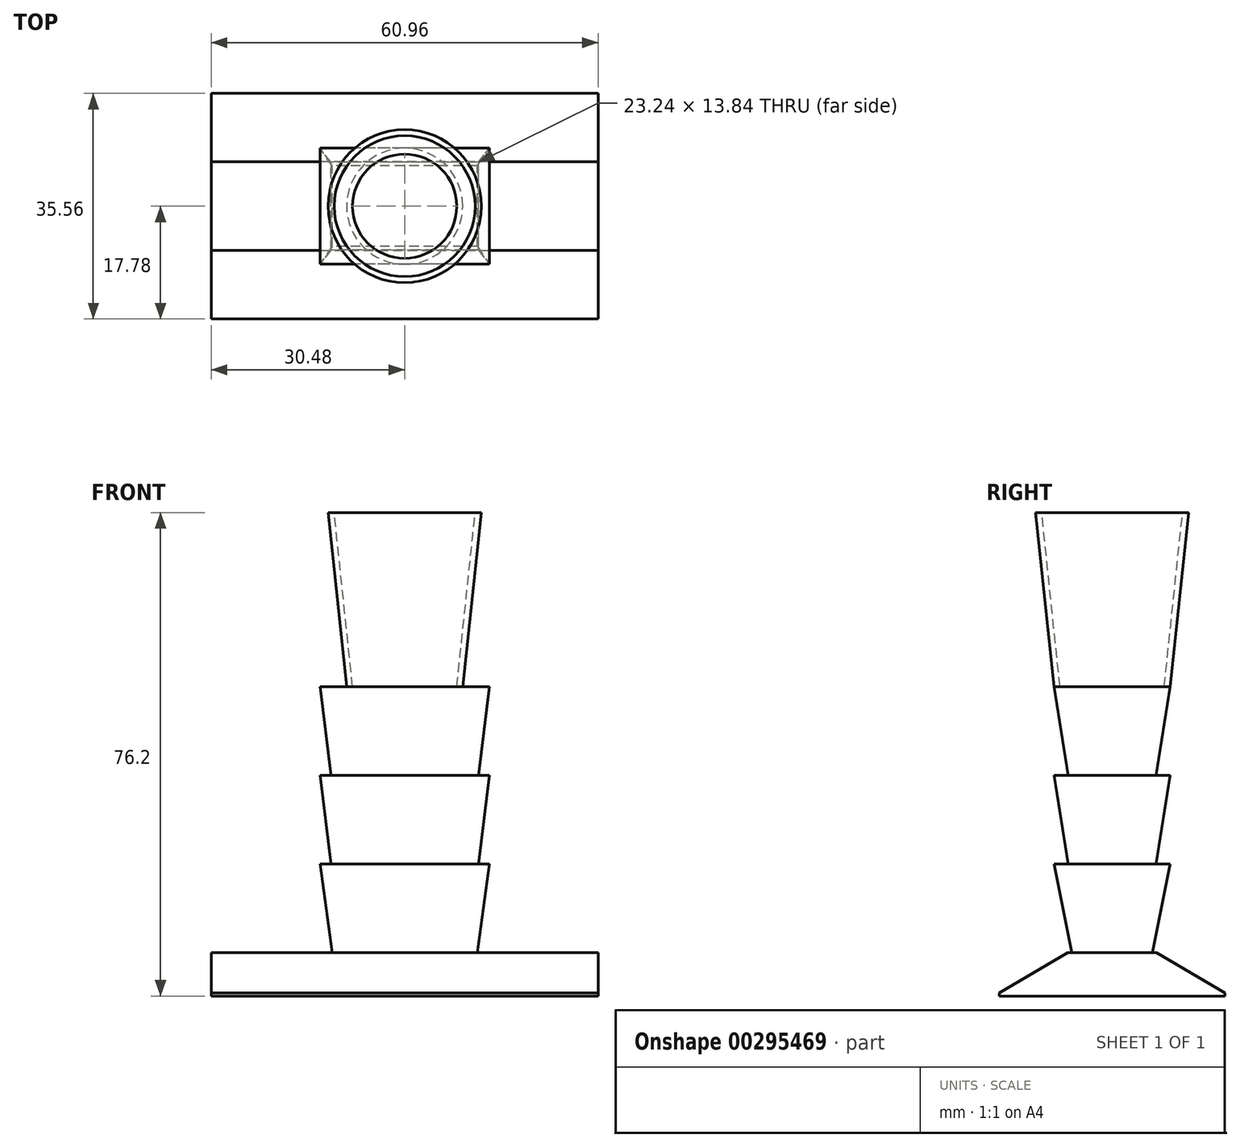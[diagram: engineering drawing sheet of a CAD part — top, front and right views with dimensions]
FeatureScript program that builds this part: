
annotation { "Feature Type Name" : "Feature", "Feature Type Description" : "" }
export const myFeature = defineFeature(function(context is Context, id is Id, definition is map)
    precondition{}
    {
        {
            var Q0;
            Q0=qCreatedBy(makeId("Top.planeOp"),FACE);
            var sketch = newSketch(context, id + "F0", { "sketchPlane" : qUnion([Q0])});
            skLineSegment(sketch, "E0.bottom", {"start": v(30.48, -17.78) * mm, "end": v(-30.48, -17.78) * mm});
            skLineSegment(sketch, "E0.top", {"start": v(30.48, 17.78) * mm, "end": v(-30.48, 17.78) * mm});
            skLineSegment(sketch, "E0.left", {"start": v(30.48, -17.78) * mm, "end": v(30.48, 17.78) * mm});
            skLineSegment(sketch, "E0.right", {"start": v(-30.48, -17.78) * mm, "end": v(-30.48, 17.78) * mm});
            skPoint(sketch, "E0.middle", {"position": v(0, 0) * mm});
            skSolve(sketch);
        }
        {
            var Q0;
            Q0=makeQuery(id+"F0.imprint","IMPRINT",FACE,{"disambiguationData":[TD([[makeQuery(id+"F0.imprint","IMPRINT",EDGE,{"derivedFrom":sQuery(id+"F0.wireOp",EDGE,"E0.bottom")}),-1.0]])]});
            extrude(context, id + "F1", {"entities" : qUnion([Q0]), "depth" : 6.86 * mm});
        }
        {
            var Q0;
            Q0=makeQuery(id+"F1.opExtrude","CAP_EDGE",EDGE,{"disambiguationData":[OSD([sQuery(id+"F0.wireOp",EDGE,"E0.top")])],"isStart":false});
            var Q1;
            Q1=makeQuery(id+"F1.opExtrude","CAP_EDGE",EDGE,{"disambiguationData":[OSD([sQuery(id+"F0.wireOp",EDGE,"E0.bottom")])],"isStart":false});
            chamfer(context, id + "F2", {"entities" : qUnion([Q0, Q1]), "chamferType" : ChamferType.TWO_OFFSETS, "width1" : 10.8 * mm, "oppositeDirection" : false, "width2" : 6.38 * mm, "tangentPropagation" : true});
        }
        {
            var Q0;
            Q0=makeQuery(id+"F1.opExtrude","CAP_FACE",FACE,{"disambiguationData":[OSD([sQuery(id+"F0.wireOp",EDGE,"E0.bottom"),sQuery(id+"F0.wireOp",EDGE,"E0.top"),sQuery(id+"F0.wireOp",EDGE,"E0.left"),sQuery(id+"F0.wireOp",EDGE,"E0.right")])],"isStart":false});
            var sketch = newSketch(context, id + "F3", { "sketchPlane" : qUnion([Q0])});
            skLineSegment(sketch, "E1.bottom", {"start": v(11.43, -6.35) * mm, "end": v(-11.43, -6.35) * mm});
            skLineSegment(sketch, "E1.top", {"start": v(11.43, 6.35) * mm, "end": v(-11.43, 6.35) * mm});
            skLineSegment(sketch, "E1.left", {"start": v(11.43, -6.35) * mm, "end": v(11.43, 6.35) * mm});
            skLineSegment(sketch, "E1.right", {"start": v(-11.43, -6.35) * mm, "end": v(-11.43, 6.35) * mm});
            skPoint(sketch, "E1.middle", {"position": v(0, 0) * mm});
            skSolve(sketch);
        }
        {
            var Q0;
            Q0=makeQuery(id+"F3.imprint","IMPRINT",FACE,{"disambiguationData":[TD([[makeQuery(id+"F3.imprint","IMPRINT",EDGE,{"derivedFrom":sQuery(id+"F3.wireOp",EDGE,"E1.bottom")}),-1.0]])]});
            cPlane(context, id + "F4", {"entities" : qUnion([Q0]), "cplaneType" : CPlaneType.OFFSET, "offset" : 13.97 * mm, "width" : 152.4 * mm, "height" : 152.4 * mm});
        }
        {
            var Q0;
            Q0=qCreatedBy(id+"F4.planeOp",FACE);
            var sketch = newSketch(context, id + "F5", { "sketchPlane" : qUnion([Q0])});
            skLineSegment(sketch, "E2.bottom", {"start": v(13.34, -9.14) * mm, "end": v(-13.34, -9.14) * mm});
            skLineSegment(sketch, "E2.top", {"start": v(13.33, 9.14) * mm, "end": v(-13.34, 9.14) * mm});
            skLineSegment(sketch, "E2.left", {"start": v(13.34, -9.14) * mm, "end": v(13.33, 9.14) * mm});
            skLineSegment(sketch, "E2.right", {"start": v(-13.33, -9.14) * mm, "end": v(-13.34, 9.14) * mm});
            skPoint(sketch, "E2.middle", {"position": v(0, 0) * mm});
            skSolve(sketch);
        }
        {
            var Q1;
            Q1=makeQuery(id+"F3.imprint","IMPRINT",FACE,{"disambiguationData":[TD([[makeQuery(id+"F3.imprint","IMPRINT",EDGE,{"derivedFrom":sQuery(id+"F3.wireOp",EDGE,"E1.bottom")}),-1.0]])]});
            var Q2;
            Q2=makeQuery(id+"F5.imprint","IMPRINT",FACE,{"disambiguationData":[TD([[makeQuery(id+"F5.imprint","IMPRINT",EDGE,{"derivedFrom":sQuery(id+"F5.wireOp",EDGE,"E2.bottom")}),-1.0]])]});
            loft(context, id + "F6", {"operationType" : NewBodyOperationType.ADD, "sheetProfilesArray" : [{ "sheetProfileEntities" : qUnion([Q1]) }, { "sheetProfileEntities" : qUnion([Q2]) }]});
        }
        {
            var Q0;
            Q0=makeQuery(id+"F6.opLoft","CAP_FACE",FACE,{"disambiguationData":[OSD([makeQuery(id+"F5.imprint","IMPRINT",FACE,{"disambiguationData":[TD([[makeQuery(id+"F5.imprint","IMPRINT",EDGE,{"derivedFrom":sQuery(id+"F5.wireOp",EDGE,"E2.bottom")}),-1.0]])]})])],"isStart":true});
            cPlane(context, id + "F7", {"entities" : qUnion([Q0]), "cplaneType" : CPlaneType.OFFSET, "offset" : 13.97 * mm, "width" : 152.4 * mm, "height" : 152.4 * mm});
        }
        {
            var Q0;
            Q0=makeQuery(id+"F6.opLoft","CAP_FACE",FACE,{"disambiguationData":[OSD([makeQuery(id+"F5.imprint","IMPRINT",FACE,{"disambiguationData":[TD([[makeQuery(id+"F5.imprint","IMPRINT",EDGE,{"derivedFrom":sQuery(id+"F5.wireOp",EDGE,"E2.bottom")}),-1.0]])]})])],"isStart":true});
            var sketch = newSketch(context, id + "F8", { "sketchPlane" : qUnion([Q0])});
            skLineSegment(sketch, "E3.bottom", {"start": v(11.62, -6.92) * mm, "end": v(-11.62, -6.92) * mm});
            skLineSegment(sketch, "E3.top", {"start": v(11.62, 6.92) * mm, "end": v(-11.62, 6.92) * mm});
            skLineSegment(sketch, "E3.left", {"start": v(11.62, -6.92) * mm, "end": v(11.62, 6.92) * mm});
            skLineSegment(sketch, "E3.right", {"start": v(-11.62, -6.92) * mm, "end": v(-11.62, 6.92) * mm});
            skPoint(sketch, "E3.middle", {"position": v(0, 0) * mm});
            skSolve(sketch);
        }
        {
            var Q0;
            Q0=qCreatedBy(id+"F7.planeOp",FACE);
            var sketch = newSketch(context, id + "F9", { "sketchPlane" : qUnion([Q0])});
            skLineSegment(sketch, "E4.bottom", {"start": v(13.33, -9.14) * mm, "end": v(-13.34, -9.14) * mm});
            skLineSegment(sketch, "E4.top", {"start": v(13.34, 9.14) * mm, "end": v(-13.34, 9.14) * mm});
            skLineSegment(sketch, "E4.left", {"start": v(13.33, -9.14) * mm, "end": v(13.33, 9.14) * mm});
            skLineSegment(sketch, "E4.right", {"start": v(-13.34, -9.14) * mm, "end": v(-13.34, 9.14) * mm});
            skPoint(sketch, "E4.middle", {"position": v(0, 0) * mm});
            skSolve(sketch);
        }
        {
            var Q1;
            Q1=makeQuery(id+"F8.imprint","IMPRINT",FACE,{"disambiguationData":[TD([[makeQuery(id+"F8.imprint","IMPRINT",EDGE,{"derivedFrom":sQuery(id+"F8.wireOp",EDGE,"E3.bottom")}),-1.0]])]});
            var Q2;
            Q2=makeQuery(id+"F9.imprint","IMPRINT",FACE,{"disambiguationData":[TD([[makeQuery(id+"F9.imprint","IMPRINT",EDGE,{"derivedFrom":sQuery(id+"F9.wireOp",EDGE,"E4.bottom")}),-1.0]])]});
            loft(context, id + "F10", {"operationType" : NewBodyOperationType.ADD, "sheetProfilesArray" : [{ "sheetProfileEntities" : qUnion([Q1]) }, { "sheetProfileEntities" : qUnion([Q2]) }]});
        }
        {
            var Q0;
            Q0=makeQuery(id+"F10.opLoft","CAP_FACE",FACE,{"disambiguationData":[OSD([makeQuery(id+"F9.imprint","IMPRINT",FACE,{"disambiguationData":[TD([[makeQuery(id+"F9.imprint","IMPRINT",EDGE,{"derivedFrom":sQuery(id+"F9.wireOp",EDGE,"E4.bottom")}),-1.0]])]})])],"isStart":true});
            cPlane(context, id + "F11", {"entities" : qUnion([Q0]), "cplaneType" : CPlaneType.OFFSET, "offset" : 13.97 * mm, "width" : 152.4 * mm, "height" : 152.4 * mm});
        }
        {
            var Q0;
            Q0=makeQuery(id+"F10.opLoft","CAP_FACE",FACE,{"disambiguationData":[OSD([makeQuery(id+"F9.imprint","IMPRINT",FACE,{"disambiguationData":[TD([[makeQuery(id+"F9.imprint","IMPRINT",EDGE,{"derivedFrom":sQuery(id+"F9.wireOp",EDGE,"E4.bottom")}),-1.0]])]})])],"isStart":true});
            var sketch = newSketch(context, id + "F12", { "sketchPlane" : qUnion([Q0])});
            skLineSegment(sketch, "E5.bottom", {"start": v(11.62, -6.92) * mm, "end": v(-11.62, -6.92) * mm});
            skLineSegment(sketch, "E5.top", {"start": v(11.62, 6.92) * mm, "end": v(-11.62, 6.92) * mm});
            skLineSegment(sketch, "E5.left", {"start": v(11.62, -6.92) * mm, "end": v(11.62, 6.92) * mm});
            skLineSegment(sketch, "E5.right", {"start": v(-11.62, -6.92) * mm, "end": v(-11.62, 6.92) * mm});
            skPoint(sketch, "E5.middle", {"position": v(0, 0) * mm});
            skSolve(sketch);
        }
        {
            var Q0;
            Q0=qCreatedBy(id+"F11.planeOp",FACE);
            var sketch = newSketch(context, id + "F13", { "sketchPlane" : qUnion([Q0])});
            skLineSegment(sketch, "E6.bottom", {"start": v(13.33, -9.14) * mm, "end": v(-13.34, -9.14) * mm});
            skLineSegment(sketch, "E6.top", {"start": v(13.33, 9.14) * mm, "end": v(-13.34, 9.14) * mm});
            skLineSegment(sketch, "E6.left", {"start": v(13.33, -9.14) * mm, "end": v(13.33, 9.14) * mm});
            skLineSegment(sketch, "E6.right", {"start": v(-13.34, -9.14) * mm, "end": v(-13.34, 9.14) * mm});
            skPoint(sketch, "E6.middle", {"position": v(0, 0) * mm});
            skSolve(sketch);
        }
        {
            var Q1;
            Q1=makeQuery(id+"F12.imprint","IMPRINT",FACE,{"disambiguationData":[TD([[makeQuery(id+"F12.imprint","IMPRINT",EDGE,{"derivedFrom":sQuery(id+"F12.wireOp",EDGE,"E5.bottom")}),-1.0]])]});
            var Q2;
            Q2=makeQuery(id+"F13.imprint","IMPRINT",FACE,{"disambiguationData":[TD([[makeQuery(id+"F13.imprint","IMPRINT",EDGE,{"derivedFrom":sQuery(id+"F13.wireOp",EDGE,"E6.bottom")}),-1.0]])]});
            loft(context, id + "F14", {"operationType" : NewBodyOperationType.ADD, "sheetProfilesArray" : [{ "sheetProfileEntities" : qUnion([Q1]) }, { "sheetProfileEntities" : qUnion([Q2]) }]});
        }
        {
            var Q0;
            Q0=makeQuery(id+"F14.opLoft","CAP_FACE",FACE,{"disambiguationData":[OSD([makeQuery(id+"F13.imprint","IMPRINT",FACE,{"disambiguationData":[TD([[makeQuery(id+"F13.imprint","IMPRINT",EDGE,{"derivedFrom":sQuery(id+"F13.wireOp",EDGE,"E6.bottom")}),-1.0]])]})])],"isStart":true});
            var sketch = newSketch(context, id + "F15", { "sketchPlane" : qUnion([Q0])});
            skLineSegment(sketch, "E7.0.0", {"start": v(13.33, -9.14) * mm, "end": v(13.33, 9.14) * mm});
            skLineSegment(sketch, "E7.0.1", {"start": v(13.33, 9.14) * mm, "end": v(-13.34, 9.14) * mm});
            skLineSegment(sketch, "E7.0.2", {"start": v(-13.34, 9.14) * mm, "end": v(-13.34, -9.14) * mm});
            skLineSegment(sketch, "E7.0.3", {"start": v(-13.34, -9.14) * mm, "end": v(13.33, -9.14) * mm});
            skCircle(sketch, "E8", {"center": v(0, 0) * mm, "radius": 9.14 * mm});
            skSolve(sketch);
        }
        {
            var Q0;
            {var subQ0=sQuery(id+"F15.wireOp",EDGE,"E7.0.2");Q0=makeQuery(id+"F15.imprint","IMPRINT",FACE,{"disambiguationData":[TD([[makeQuery(id+"F15.imprint","IMPRINT",EDGE,{"derivedFrom":subQ0}),1.0]])]});}
            cPlane(context, id + "F16", {"entities" : qUnion([Q0]), "cplaneType" : CPlaneType.OFFSET, "offset" : 27.43 * mm, "width" : 152.4 * mm, "height" : 152.4 * mm});
        }
        {
            var Q0;
            Q0=qCreatedBy(id+"F16.planeOp",FACE);
            var sketch = newSketch(context, id + "F17", { "sketchPlane" : qUnion([Q0])});
            skCircle(sketch, "E9", {"center": v(0, 0) * mm, "radius": 12.07 * mm});
            skSolve(sketch);
        }
        {
            var Q1;
            {var subQ0=sQuery(id+"F15.wireOp",EDGE,"E8");var subQ1=makeQuery(id+"F15.imprint","INTERSECT",VERTEX,{"derivedFrom":[sQuery(id+"F15.wireOp",EDGE,"E7.0.1"),subQ0]});Q1=makeQuery(id+"F15.imprint","IMPRINT",FACE,{"disambiguationData":[TD([[makeQuery(id+"F15.imprint","IMPRINT",EDGE,{"disambiguationData":[TD([[subQ1,-1.0]])],"derivedFrom":subQ0}),1.0]])]});}
            var Q2;
            Q2=makeQuery(id+"F17.imprint","IMPRINT",FACE,{"disambiguationData":[TD([[makeQuery(id+"F17.imprint","IMPRINT",EDGE,{"derivedFrom":sQuery(id+"F17.wireOp",EDGE,"E9")}),1.0]])]});
            loft(context, id + "F18", {"operationType" : NewBodyOperationType.ADD, "sheetProfilesArray" : [{ "sheetProfileEntities" : qUnion([Q1]) }, { "sheetProfileEntities" : qUnion([Q2]) }]});
        }
        {
            var Q0;
            Q0=makeQuery(id+"F18.opLoft","CAP_FACE",FACE,{"disambiguationData":[OSD([makeQuery(id+"F17.imprint","IMPRINT",FACE,{"disambiguationData":[TD([[makeQuery(id+"F17.imprint","IMPRINT",EDGE,{"derivedFrom":sQuery(id+"F17.wireOp",EDGE,"E9")}),1.0]])]})])],"isStart":true});
            var sketch = newSketch(context, id + "F19", { "sketchPlane" : qUnion([Q0])});
            skCircle(sketch, "E10.0.0", {"center": v(0, 0) * mm, "radius": 12.07 * mm});
            skCircle(sketch, "E11.0", {"center": v(0, 0) * mm, "radius": 11.1 * mm});
            skSolve(sketch);
        }
        {
            var Q0;
            Q0=makeQuery(id+"F19.imprint","IMPRINT",FACE,{"disambiguationData":[TD([[makeQuery(id+"F19.imprint","IMPRINT",EDGE,{"derivedFrom":sQuery(id+"F19.wireOp",EDGE,"E11.0")}),1.0]])]});
            var Q1;
            {var subQ0=sQuery(id+"F13.wireOp",EDGE,"E6.right");var subQ2=sQuery(id+"F13.wireOp",EDGE,"E6.top");var subQ3=sQuery(id+"F12.wireOp",EDGE,"E5.right");var subQ5=sQuery(id+"F12.wireOp",EDGE,"E5.top");var subQ6=sQuery(id+"F13.wireOp",EDGE,"E6.bottom");var subQ7=sQuery(id+"F12.wireOp",EDGE,"E5.bottom");var subQ8=makeQuery(id+"F14.opLoft","CAP_FACE",FACE,{"disambiguationData":[OSD([makeQuery(id+"F13.imprint","IMPRINT",FACE,{"disambiguationData":[TD([[makeQuery(id+"F13.imprint","IMPRINT",EDGE,{"derivedFrom":subQ6}),-1.0]])]})])],"isStart":true});Q1=makeQuery(id+"F18.boolean.opBoolean","SPLIT",FACE,{"disambiguationData":[TD([makeQuery(id+"F14.opLoft","SWEPT_FACE",FACE,{"disambiguationData":[OSD([subQ7,subQ5,subQ3,subQ6,subQ2,subQ0])]})])],"derivedFrom":subQ8});}
            extrude(context, id + "F20", {"entities" : qUnion([Q0]), "operationType" : NewBodyOperationType.REMOVE, "endBound" : BoundingType.UP_TO_SURFACE, "oppositeDirection" : true, "endBoundEntityFace" : qUnion([Q1]), "depth" : 25.4 * mm, "hasDraft" : true, "draftAngle" : 6 * degree, "draftPullDirection" : true});
        }
    });
